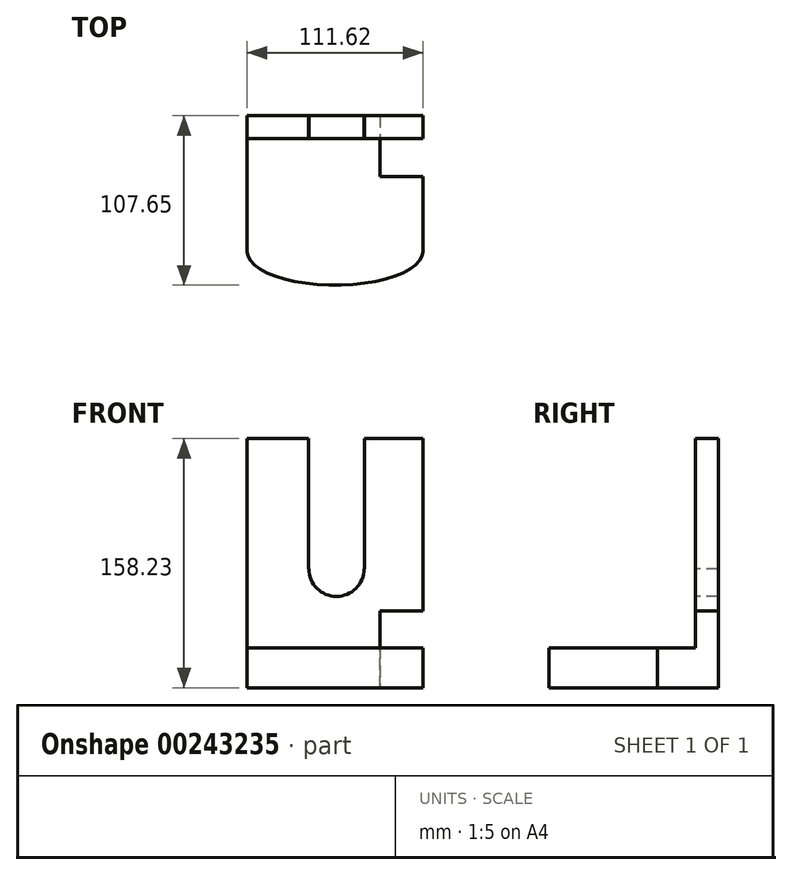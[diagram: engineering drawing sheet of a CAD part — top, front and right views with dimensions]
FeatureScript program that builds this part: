
annotation { "Feature Type Name" : "Feature", "Feature Type Description" : "" }
export const myFeature = defineFeature(function(context is Context, id is Id, definition is map)
    precondition{}
    {
        {
            var Q0;
            Q0=qCreatedBy(makeId("Top.planeOp"),FACE);
            var sketch = newSketch(context, id + "F0", { "sketchPlane" : qUnion([Q0])});
            skLineSegment(sketch, "E0.bottom", {"start": v(-53.72, -24.2) * mm, "end": v(57.9, -24.2) * mm});
            skLineSegment(sketch, "E0.top", {"start": v(-53.72, 62.17) * mm, "end": v(57.9, 62.17) * mm});
            skLineSegment(sketch, "E0.left", {"start": v(-53.72, -24.2) * mm, "end": v(-53.72, 62.17) * mm});
            skLineSegment(sketch, "E0.right", {"start": v(57.9, -24.2) * mm, "end": v(57.9, 62.17) * mm});
            skSolve(sketch);
        }
        {
            var Q0;
            Q0=makeQuery(id+"F0.imprint","IMPRINT",FACE,{"disambiguationData":[TD([[makeQuery(id+"F0.imprint","IMPRINT",EDGE,{"derivedFrom":sQuery(id+"F0.wireOp",EDGE,"E0.bottom")}),1.0]])]});
            extrude(context, id + "F1", {"entities" : qUnion([Q0]), "depth" : 25.4 * mm});
        }
        {
            var Q0;
            Q0=makeQuery(id+"F1.opExtrude","SWEPT_FACE",FACE,{"disambiguationData":[OSD([sQuery(id+"F0.wireOp",EDGE,"E0.top")])]});
            var sketch = newSketch(context, id + "F2", { "sketchPlane" : qUnion([Q0])});
            skLineSegment(sketch, "E1", {"start": v(-57.9, 25.4) * mm, "end": v(-57.9, 158.23) * mm});
            skLineSegment(sketch, "E2", {"start": v(53.72, 25.4) * mm, "end": v(53.72, 158.23) * mm});
            skLineSegment(sketch, "E3", {"start": v(53.72, 158.23) * mm, "end": v(-57.9, 158.23) * mm});
            skSolve(sketch);
        }
        {
            var Q0;
            Q0=makeQuery(id+"F2.imprint","IMPRINT",FACE,{"disambiguationData":[TD([[makeQuery(id+"F2.imprint","IMPRINT",EDGE,{"derivedFrom":sQuery(id+"F2.wireOp",EDGE,"E1")}),-1.0]])]});
            extrude(context, id + "F3", {"entities" : qUnion([Q0]), "operationType" : NewBodyOperationType.ADD, "oppositeDirection" : true, "depth" : 14.48 * mm});
        }
        {
            var Q0;
            Q0=makeQuery(id+"F1.opExtrude","CAP_FACE",FACE,{"disambiguationData":[OSD([sQuery(id+"F0.wireOp",EDGE,"E0.bottom"),sQuery(id+"F0.wireOp",EDGE,"E0.top"),sQuery(id+"F0.wireOp",EDGE,"E0.left"),sQuery(id+"F0.wireOp",EDGE,"E0.right")])],"isStart":false});
            var sketch = newSketch(context, id + "F4", { "sketchPlane" : qUnion([Q0])});
            skEllipse(sketch, "E4", {"center": v(2.09, -24.2) * mm, "majorRadius": 55.8 * mm, "minorRadius": 21.28 * mm, "majorAxis": v(1, 0)});
            skSolve(sketch);
        }
        {
            var Q0;
            {var subQ1=makeQuery(id+"F1.opExtrude","CAP_EDGE",EDGE,{"disambiguationData":[OSD([sQuery(id+"F0.wireOp",EDGE,"E0.bottom")])],"isStart":false});Q0=makeQuery(id+"F4.imprint","IMPRINT",FACE,{"disambiguationData":[TD([[makeQuery(id+"F4.imprint","IMPRINT",EDGE,{"derivedFrom":subQ1}),-1.0]])]});}
            extrude(context, id + "F5", {"entities" : qUnion([Q0]), "operationType" : NewBodyOperationType.ADD, "oppositeDirection" : true, "depth" : 25.4 * mm});
        }
        {
            var Q0;
            {var subQ0=sQuery(id+"F0.wireOp",EDGE,"E0.bottom");Q0=makeQuery(id+"F5.boolean.opBoolean","MERGE",FACE,{"derivedFrom":[makeQuery(id+"F1.opExtrude","CAP_FACE",FACE,{"disambiguationData":[OSD([subQ0,sQuery(id+"F0.wireOp",EDGE,"E0.top"),sQuery(id+"F0.wireOp",EDGE,"E0.left"),sQuery(id+"F0.wireOp",EDGE,"E0.right")])],"isStart":false}),makeQuery(id+"F5.opExtrude","CAP_FACE",FACE,{"disambiguationData":[OSD([subQ0,sQuery(id+"F4.wireOp",EDGE,"E4")])],"isStart":true})]});}
            var sketch = newSketch(context, id + "F6", { "sketchPlane" : qUnion([Q0])});
            skLineSegment(sketch, "E5", {"start": v(57.9, 23.57) * mm, "end": v(30.6, 23.57) * mm});
            skLineSegment(sketch, "E6", {"start": v(57.9, 70.44) * mm, "end": v(57.9, 23.57) * mm});
            skLineSegment(sketch, "E7", {"start": v(30.6, 23.57) * mm, "end": v(30.6, 70.44) * mm});
            skLineSegment(sketch, "E8", {"start": v(30.6, 70.44) * mm, "end": v(57.9, 70.44) * mm});
            skSolve(sketch);
        }
        {
            var Q0;
            {var subQ0=sQuery(id+"F6.wireOp",EDGE,"E5");Q0=makeQuery(id+"F6.imprint","IMPRINT",FACE,{"disambiguationData":[TD([[makeQuery(id+"F6.imprint","IMPRINT",EDGE,{"derivedFrom":subQ0}),-1.0]])]});}
            var Q1;
            {var subQ3=sQuery(id+"F6.wireOp",EDGE,"E8");Q1=makeQuery(id+"F6.imprint","IMPRINT",FACE,{"disambiguationData":[TD([[makeQuery(id+"F6.imprint","IMPRINT",EDGE,{"derivedFrom":subQ3}),-1.0]])]});}
            extrude(context, id + "F7", {"entities" : qUnion([Q0, Q1]), "operationType" : NewBodyOperationType.REMOVE, "oppositeDirection" : true, "depth" : 56.13 * mm});
        }
        {
            var Q0;
            Q0=makeQuery(id+"F3.opExtrude","CAP_FACE",FACE,{"disambiguationData":[OSD([sQuery(id+"F0.wireOp",EDGE,"E0.top"),sQuery(id+"F2.wireOp",EDGE,"E1"),sQuery(id+"F2.wireOp",EDGE,"E2"),sQuery(id+"F2.wireOp",EDGE,"E3")])],"isStart":false});
            var sketch = newSketch(context, id + "F8", { "sketchPlane" : qUnion([Q0])});
            skLineSegment(sketch, "E9", {"start": v(30.6, 25.4) * mm, "end": v(30.6, 48.7) * mm});
            skLineSegment(sketch, "E10", {"start": v(30.6, 48.7) * mm, "end": v(57.9, 48.7) * mm});
            skLineSegment(sketch, "E11", {"start": v(57.9, 48.7) * mm, "end": v(57.9, 25.4) * mm});
            skLineSegment(sketch, "E12", {"start": v(57.9, 25.4) * mm, "end": v(30.6, 25.4) * mm});
            skSolve(sketch);
        }
        {
            var Q0;
            Q0=makeQuery(id+"F8.imprint","IMPRINT",FACE,{"disambiguationData":[TD([[makeQuery(id+"F8.imprint","IMPRINT",EDGE,{"derivedFrom":sQuery(id+"F8.wireOp",EDGE,"E9")}),-1.0]])]});
            extrude(context, id + "F9", {"entities" : qUnion([Q0]), "operationType" : NewBodyOperationType.REMOVE, "oppositeDirection" : true, "depth" : 25.4 * mm});
        }
        {
            var Q0;
            Q0=makeQuery(id+"F3.opExtrude","CAP_FACE",FACE,{"disambiguationData":[OSD([sQuery(id+"F0.wireOp",EDGE,"E0.top"),sQuery(id+"F2.wireOp",EDGE,"E1"),sQuery(id+"F2.wireOp",EDGE,"E2"),sQuery(id+"F2.wireOp",EDGE,"E3")])],"isStart":false});
            var sketch = newSketch(context, id + "F10", { "sketchPlane" : qUnion([Q0])});
            skLineSegment(sketch, "E13", {"start": v(-14.68, 167.22) * mm, "end": v(-14.68, 75.55) * mm});
            skLineSegment(sketch, "E14", {"start": v(-14.68, 75.55) * mm, "end": v(20.74, 75.55) * mm});
            skLineSegment(sketch, "E15", {"start": v(20.74, 75.55) * mm, "end": v(20.74, 168.96) * mm});
            skLineSegment(sketch, "E16", {"start": v(20.74, 168.96) * mm, "end": v(-14.68, 167.22) * mm});
            skSolve(sketch);
        }
        {
            var Q0;
            {var subQ0=sQuery(id+"F10.wireOp",EDGE,"E14");Q0=makeQuery(id+"F10.imprint","IMPRINT",FACE,{"disambiguationData":[TD([[makeQuery(id+"F10.imprint","IMPRINT",EDGE,{"derivedFrom":subQ0}),1.0]])]});}
            extrude(context, id + "F11", {"entities" : qUnion([Q0]), "operationType" : NewBodyOperationType.REMOVE, "oppositeDirection" : true, "depth" : 25.4 * mm});
        }
        {
            var Q0;
            Q0=makeQuery(id+"F3.opExtrude","CAP_FACE",FACE,{"disambiguationData":[OSD([sQuery(id+"F0.wireOp",EDGE,"E0.top"),sQuery(id+"F2.wireOp",EDGE,"E1"),sQuery(id+"F2.wireOp",EDGE,"E2"),sQuery(id+"F2.wireOp",EDGE,"E3")])],"isStart":false});
            var sketch = newSketch(context, id + "F12", { "sketchPlane" : qUnion([Q0])});
            skCircle(sketch, "E17", {"center": v(3.03, 75.55) * mm, "radius": 17.5 * mm});
            skSolve(sketch);
        }
        {
            var Q0;
            {var subQ0=sQuery(id+"F12.wireOp",EDGE,"E17");var subQ1=makeQuery(id+"F11.boolean.opBoolean","COPY",EDGE,{"derivedFrom":makeQuery(id+"F11.opExtrude","CAP_EDGE",EDGE,{"disambiguationData":[OSD([sQuery(id+"F10.wireOp",EDGE,"E14")])],"isStart":true})});var subQ2=makeQuery(id+"F12.imprint","INTERSECT",VERTEX,{"disambiguationData":[OD(0.0)],"derivedFrom":[subQ1,subQ0]});Q0=makeQuery(id+"F12.imprint","IMPRINT",FACE,{"disambiguationData":[TD([[makeQuery(id+"F12.imprint","IMPRINT",EDGE,{"disambiguationData":[TD([[subQ2,-1.0]])],"derivedFrom":subQ0}),1.0]])]});}
            extrude(context, id + "F13", {"entities" : qUnion([Q0]), "operationType" : NewBodyOperationType.REMOVE, "oppositeDirection" : true, "depth" : 25.4 * mm});
        }
    });
